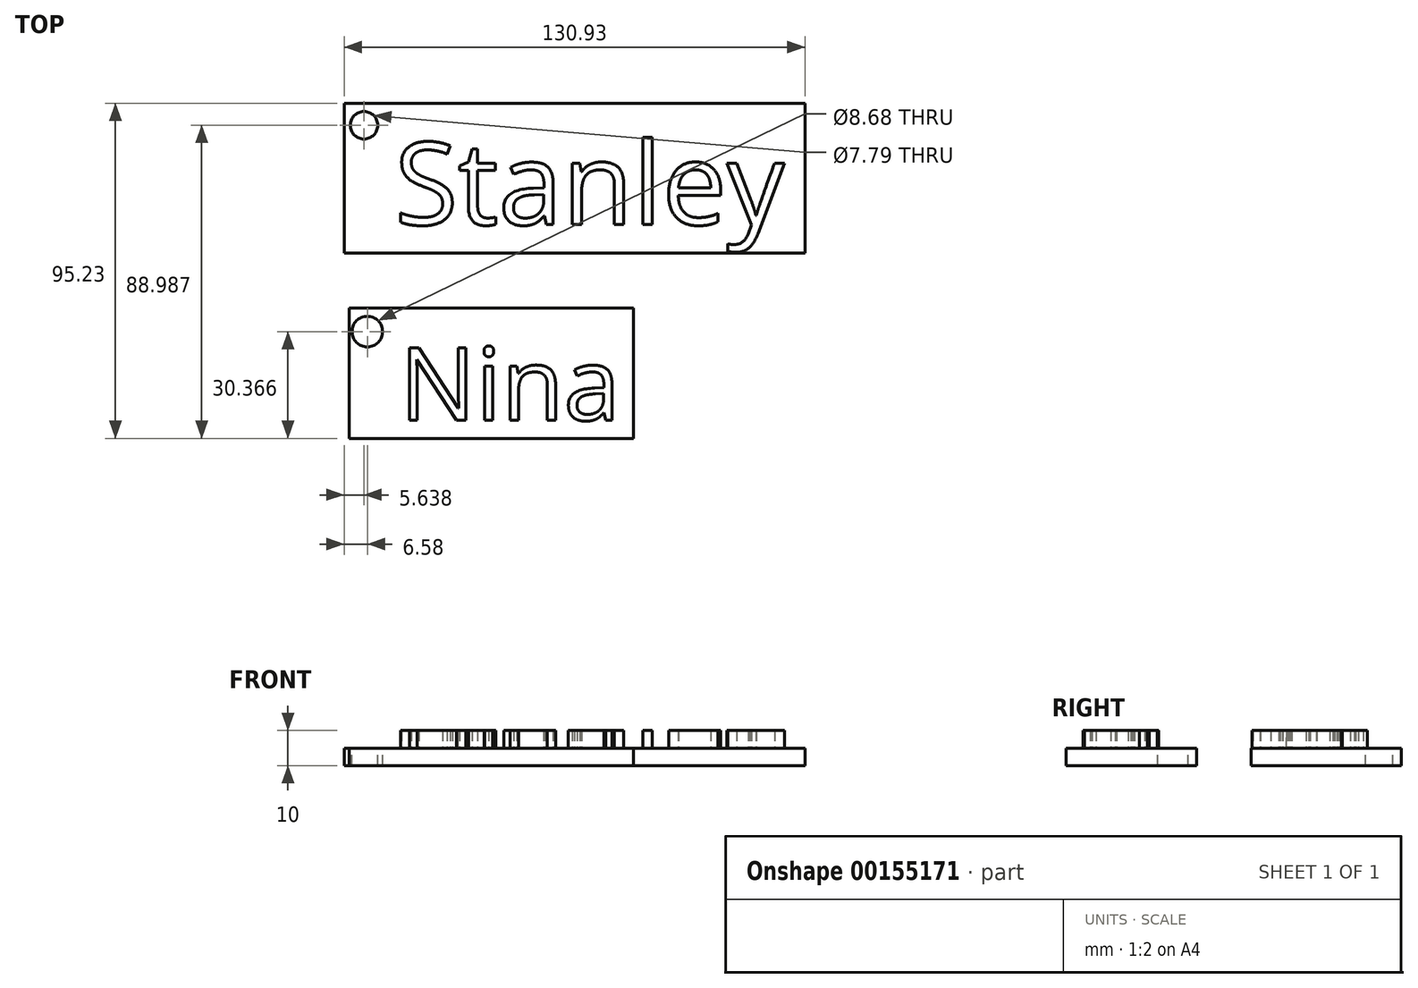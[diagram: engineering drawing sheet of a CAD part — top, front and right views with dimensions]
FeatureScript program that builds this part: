
annotation { "Feature Type Name" : "Feature", "Feature Type Description" : "" }
export const myFeature = defineFeature(function(context is Context, id is Id, definition is map)
    precondition{}
    {
        {
            var Q0;
            Q0=qCreatedBy(makeId("Top.planeOp"),FACE);
            var sketch = newSketch(context, id + "F0", { "sketchPlane" : qUnion([Q0])});
            skLineSegment(sketch, "E0.bottom", {"start": v(-59.08, 52.74) * mm, "end": v(53.1, 52.74) * mm});
            skLineSegment(sketch, "E0.top", {"start": v(-59.08, 11.12) * mm, "end": v(53.1, 11.12) * mm});
            skLineSegment(sketch, "E0.left", {"start": v(-59.08, 52.74) * mm, "end": v(-59.08, 11.12) * mm});
            skLineSegment(sketch, "E0.right", {"start": v(53.1, 52.74) * mm, "end": v(53.1, 11.12) * mm});
            skSolve(sketch);
        }
        {
            var Q0;
            Q0=makeQuery(id+"F0.imprint","IMPRINT",FACE,{"disambiguationData":[TD([[makeQuery(id+"F0.imprint","IMPRINT",EDGE,{"derivedFrom":sQuery(id+"F0.wireOp",EDGE,"E0.bottom")}),-1.0]])]});
            extrude(context, id + "F1", {"entities" : qUnion([Q0]), "depth" : 5 * mm});
        }
        {
            var Q0;
            {var subQ0=sQuery(id+"F0.wireOp",EDGE,"E0.right");var subQ1=sQuery(id+"F0.wireOp",EDGE,"E0.left");var subQ2=sQuery(id+"F0.wireOp",EDGE,"E0.top");var subQ3=sQuery(id+"F0.wireOp",EDGE,"E0.bottom");Q0=makeQuery(id+"FSdAYOAr6HNSi85_1.boolean.opBoolean","SPLIT",FACE,{"disambiguationData":[TD([makeQuery(id+"F1.opExtrude","SWEPT_FACE",FACE,{"disambiguationData":[OSD([subQ3])]})])],"derivedFrom":makeQuery(id+"FTzVNkmaZcNYXl3_1.boolean.opBoolean","MERGE",FACE,{"derivedFrom":[makeQuery(id+"F1.opExtrude","CAP_FACE",FACE,{"disambiguationData":[OSD([subQ3,subQ2,subQ1,subQ0])],"isStart":false}),makeQuery(id+"FTzVNkmaZcNYXl3_1.opExtrude","SWEPT_FACE",FACE,{"disambiguationData":[OSD([subQ0]),TDD([makeQuery(id+"F1.opExtrude","CAP_EDGE",EDGE,{"disambiguationData":[OSD([subQ0])],"isStart":false})])]})]})});}
            var sketch = newSketch(context, id + "F2", { "sketchPlane" : qUnion([Q0])});
            skCircle(sketch, "E1", {"center": v(-53.44, 46.5) * mm, "radius": 3.9 * mm});
            skSolve(sketch);
        }
        {
            var Q0;
            Q0 = qSketchRegion(id + "F2", true);
            extrude(context, id + "F3", {"entities" : qUnion([Q0]), "operationType" : NewBodyOperationType.REMOVE, "oppositeDirection" : true, "depth" : 25 * mm});
        }
        {
            var Q0;
            Q0=makeQuery(id+"F1.opExtrude","CAP_FACE",FACE,{"disambiguationData":[OSD([sQuery(id+"F0.wireOp",EDGE,"E0.bottom"),sQuery(id+"F0.wireOp",EDGE,"E0.top"),sQuery(id+"F0.wireOp",EDGE,"E0.left"),sQuery(id+"F0.wireOp",EDGE,"E0.right")])],"isStart":false});
            var sketch = newSketch(context, id + "F4", { "sketchPlane" : qUnion([Q0])});
            skText(sketch, "E2", { "text": "Stanley", "fontName": "OpenSans-Regular.ttf"});
            const initialGuessF4  = {"E2": [-0.04473, 0.01825, 1, 0, 0.02354]};
            skSetInitialGuess(sketch, initialGuessF4);
            skSolve(sketch);
        }
        {
            var Q0;
            Q0=makeQuery(id+"F1.opExtrude","SWEPT_FACE",FACE,{"disambiguationData":[OSD([sQuery(id+"F0.wireOp",EDGE,"E0.right")])]});
            extrude(context, id + "F5", {"entities" : qUnion([Q0]), "operationType" : NewBodyOperationType.ADD, "depth" : 18.75 * mm});
        }
        {
            var Q0;
            Q0 = qSketchRegion(id + "F4", true);
            extrude(context, id + "F6", {"entities" : qUnion([Q0]), "operationType" : NewBodyOperationType.ADD, "depth" : 5 * mm});
        }
        {
            var Q0;
            {var subQ0=sQuery(id+"F0.wireOp",EDGE,"E0.top");Q0=makeQuery(id+"F5.boolean.opBoolean","MERGE",FACE,{"derivedFrom":[makeQuery(id+"F1.opExtrude","SWEPT_FACE",FACE,{"disambiguationData":[OSD([subQ0])]}),makeQuery(id+"F5.opExtrude","SWEPT_FACE",FACE,{"disambiguationData":[OSD([subQ0,sQuery(id+"F0.wireOp",EDGE,"E0.right")])]})]});}
            extrude(context, id + "F7", {"entities" : qUnion([Q0]), "operationType" : NewBodyOperationType.ADD, "depth" : 1 * mm});
        }
        {
            var Q0;
            Q0=qCreatedBy(makeId("Top.planeOp"),FACE);
            var sketch = newSketch(context, id + "F8", { "sketchPlane" : qUnion([Q0])});
            skLineSegment(sketch, "E3.bottom", {"start": v(-57.68, -7.42) * mm, "end": v(70.86, -7.42) * mm});
            skLineSegment(sketch, "E3.top", {"start": v(-57.68, -42.5) * mm, "end": v(70.86, -42.5) * mm});
            skLineSegment(sketch, "E3.left", {"start": v(-57.68, -7.42) * mm, "end": v(-57.68, -42.5) * mm});
            skLineSegment(sketch, "E3.right", {"start": v(70.86, -7.42) * mm, "end": v(70.86, -42.5) * mm});
            skSolve(sketch);
        }
        {
            var Q0;
            Q0=makeQuery(id+"F8.imprint","IMPRINT",FACE,{"disambiguationData":[TD([[makeQuery(id+"F8.imprint","IMPRINT",EDGE,{"derivedFrom":sQuery(id+"F8.wireOp",EDGE,"E3.bottom")}),-1.0]])]});
            extrude(context, id + "F9", {"entities" : qUnion([Q0]), "depth" : 5 * mm});
        }
        {
            var Q0;
            Q0=makeQuery(id+"F9.opExtrude","CAP_FACE",FACE,{"disambiguationData":[OSD([sQuery(id+"F8.wireOp",EDGE,"E3.bottom"),sQuery(id+"F8.wireOp",EDGE,"E3.top"),sQuery(id+"F8.wireOp",EDGE,"E3.left"),sQuery(id+"F8.wireOp",EDGE,"E3.right")])],"isStart":false});
            var sketch = newSketch(context, id + "F10", { "sketchPlane" : qUnion([Q0])});
            skCircle(sketch, "E4", {"center": v(-52.5, -12.12) * mm, "radius": 4.34 * mm});
            skSolve(sketch);
        }
        {
            var Q0;
            Q0=makeQuery(id+"F10.imprint","IMPRINT",FACE,{"disambiguationData":[TD([[makeQuery(id+"F10.imprint","IMPRINT",EDGE,{"derivedFrom":sQuery(id+"F10.wireOp",EDGE,"E4")}),1.0]])]});
            extrude(context, id + "F11", {"entities" : qUnion([Q0]), "operationType" : NewBodyOperationType.REMOVE, "oppositeDirection" : true, "depth" : 25 * mm});
        }
        {
            var Q0;
            Q0=makeQuery(id+"F9.opExtrude","SWEPT_FACE",FACE,{"disambiguationData":[OSD([sQuery(id+"F8.wireOp",EDGE,"E3.bottom")])]});
            extrude(context, id + "F12", {"entities" : qUnion([Q0]), "operationType" : NewBodyOperationType.ADD, "depth" : 2 * mm});
        }
        {
            var Q0;
            {var subQ0=sQuery(id+"F8.wireOp",EDGE,"E3.bottom");Q0=makeQuery(id+"F12.boolean.opBoolean","MERGE",FACE,{"derivedFrom":[makeQuery(id+"F9.opExtrude","CAP_FACE",FACE,{"disambiguationData":[OSD([subQ0,sQuery(id+"F8.wireOp",EDGE,"E3.top"),sQuery(id+"F8.wireOp",EDGE,"E3.left"),sQuery(id+"F8.wireOp",EDGE,"E3.right")])],"isStart":false}),makeQuery(id+"F12.opExtrude","SWEPT_FACE",FACE,{"disambiguationData":[OSD([subQ0]),TDD([makeQuery(id+"F9.opExtrude","CAP_EDGE",EDGE,{"disambiguationData":[OSD([subQ0])],"isStart":false})])]})]});}
            var sketch = newSketch(context, id + "F13", { "sketchPlane" : qUnion([Q0])});
            skText(sketch, "E5", { "text": "Nina", "fontName": "OpenSans-Regular.ttf"});
            const initialGuessF13  = {"E5": [-0.04332, -0.03732, 1, 0, 0.02072]};
            skSetInitialGuess(sketch, initialGuessF13);
            skSolve(sketch);
        }
        {
            var Q0;
            Q0 = qSketchRegion(id + "F13", true);
            extrude(context, id + "F14", {"entities" : qUnion([Q0]), "operationType" : NewBodyOperationType.ADD, "depth" : 5 * mm});
        }
        {
            var Q0;
            {var subQ0=sQuery(id+"F8.wireOp",EDGE,"E3.right");Q0=makeQuery(id+"F12.boolean.opBoolean","MERGE",FACE,{"derivedFrom":[makeQuery(id+"F9.opExtrude","SWEPT_FACE",FACE,{"disambiguationData":[OSD([subQ0])]}),makeQuery(id+"F12.opExtrude","SWEPT_FACE",FACE,{"disambiguationData":[OSD([sQuery(id+"F8.wireOp",EDGE,"E3.bottom"),subQ0])]})]});}
            extrude(context, id + "F15", {"entities" : qUnion([Q0]), "operationType" : NewBodyOperationType.REMOVE, "oppositeDirection" : true, "depth" : 47.75 * mm});
        }
    });
